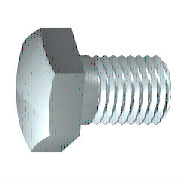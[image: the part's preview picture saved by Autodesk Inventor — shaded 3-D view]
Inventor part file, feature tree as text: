
AUTODESK INVENTOR PART (.ipt)
format: ipt  version: 2020 (Build 240168000, 168)  size: 188,928 bytes
history: native  units: mm (DEFAULTED — no unit token found)
features: sketch x3, extrude x1, chamfer x1, plane x1
ambient origin geometry x7: Origin, YZ Plane, XZ Plane, X Axis, Y Axis, Z Axis, Center Point
bodies: Solid1 (feature_tree), Body (feature_tree)
feature tree (6):
  extrude  "Head"  Depth=57.9mm
  chamfer  "Chamfer1"  Distance=2.4mm
  plane  "Work Plane1"
  sketch  "Sketch1"  dims[d0=60.0mm d1=57.9mm]
  sketch  "Sketch2"  dims[d2=4.0mm]
  sketch  "Sketch4"  dims[d12=90.0deg d3=2.4mm d4=0.0mm d5=30.0deg d21=90.0deg d6=0.429415mm d7=0.429515mm d8=0.0mm d9=0.4001mm d10=5.9mm d11=7.0mm d13=0.429515mm d14=3.621114mm d15=57.9mm d16=0.0mm d19=7.0mm d55=45.0deg d57=0.0mm d58=0.0mm]
